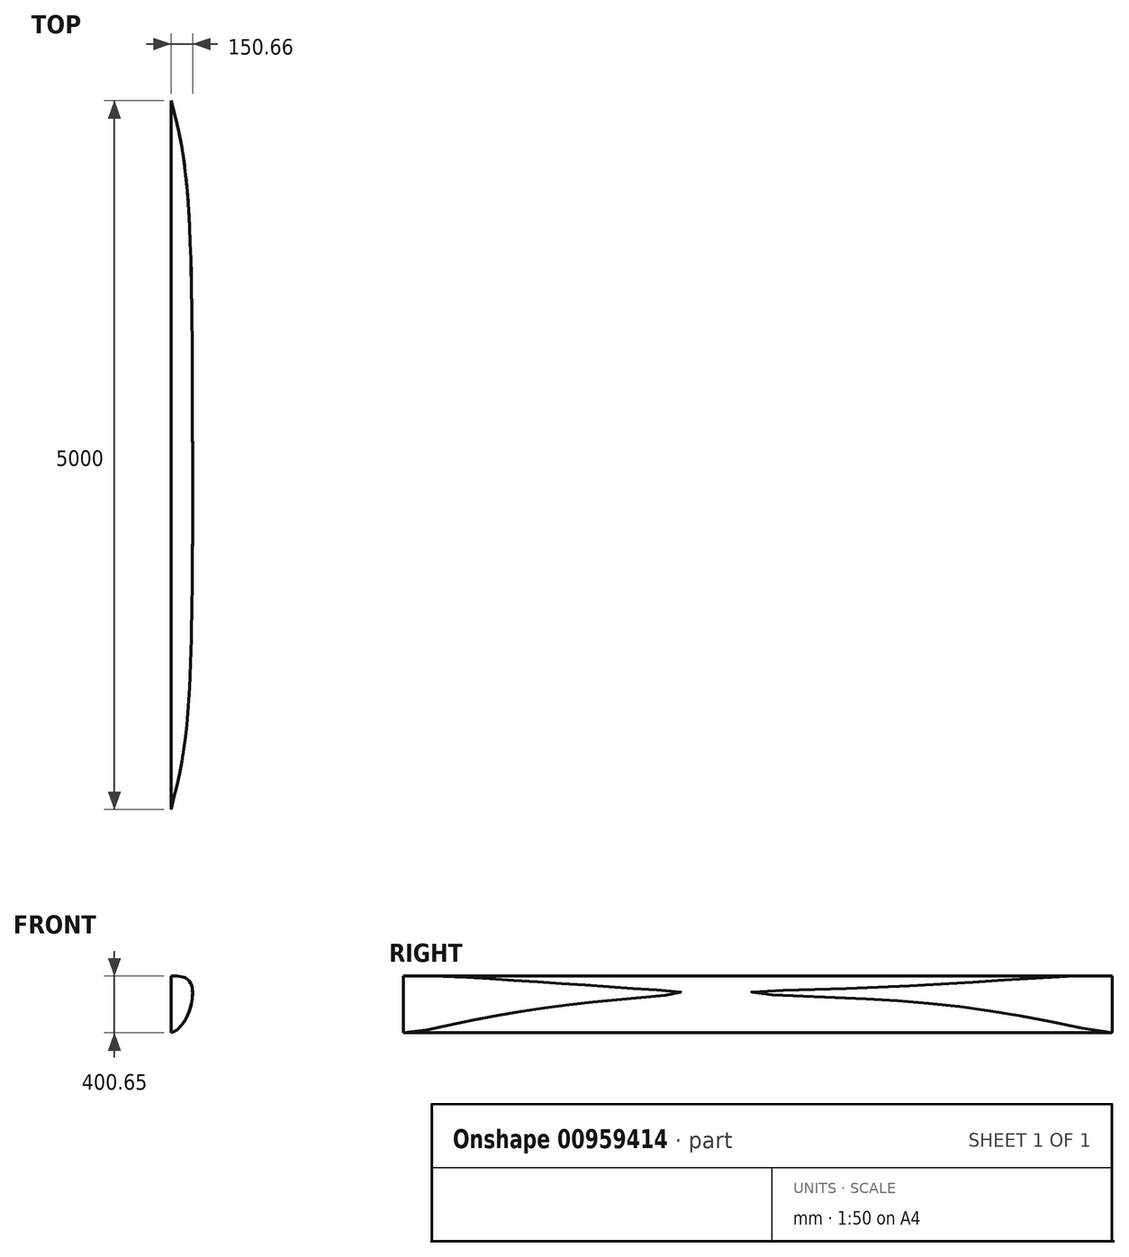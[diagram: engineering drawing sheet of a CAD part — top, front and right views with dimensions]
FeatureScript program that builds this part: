
annotation { "Feature Type Name" : "Feature", "Feature Type Description" : "" }
export const myFeature = defineFeature(function(context is Context, id is Id, definition is map)
    precondition{}
    {
        {
            var Q0;
            Q0=qCreatedBy(makeId("Top.planeOp"),FACE);
            var sketch = newSketch(context, id + "F0", { "sketchPlane" : qUnion([Q0])});
            skLineSegment(sketch, "E0", {"start": v(0, 0) * mm, "end": v(0, -2700) * mm});
            skLineSegment(sketch, "E1", {"start": v(0, 0) * mm, "end": v(0, 2300) * mm});
            skLineSegment(sketch, "E2", {"start": v(0, 1800) * mm, "end": v(100, 1800) * mm, "construction": true});
            skLineSegment(sketch, "E3", {"start": v(0, -2200) * mm, "end": v(100, -2200) * mm, "construction": true});
            skLineSegment(sketch, "E4", {"start": v(0, 0) * mm, "end": v(150, 0) * mm, "construction": true});
            skSolve(sketch);
        }
        {
            var Q0;
            Q0=qCreatedBy(makeId("Right.planeOp"),FACE);
            var sketch = newSketch(context, id + "F1", { "sketchPlane" : qUnion([Q0])});
            skLineSegment(sketch, "E5", {"start": v(0, 0) * mm, "end": v(0, -300) * mm, "construction": true});
            skLineSegment(sketch, "E6", {"start": v(1800, 0) * mm, "end": v(1800, -250) * mm, "construction": true});
            skLineSegment(sketch, "E7", {"start": v(-2200, 0) * mm, "end": v(-2200, -250) * mm, "construction": true});
            skSolve(sketch);
        }
        {
            var Q0;
            Q0=qCreatedBy(makeId("Front.planeOp"),FACE);
            var sketch = newSketch(context, id + "F2", { "sketchPlane" : qUnion([Q0])});
            skFitSpline(sketch, "E8", {"points": [v(0, 100) * mm, v(95, 90) * mm, v(150, 0) * mm, v(0, -300) * mm], "startDerivative": vector(370.55, 15) * mm, "endDerivative": vector(-679.9, -235.19) * mm});
            skLineSegment(sketch, "E9", {"start": v(0, 100) * mm, "end": v(0, -300) * mm});
            skLineSegment(sketch, "E10", {"start": v(0, 100) * mm, "end": v(0, 90) * mm, "construction": true});
            skLineSegment(sketch, "E11", {"start": v(0, 90) * mm, "end": v(95, 90) * mm, "construction": true});
            skSolve(sketch);
        }
        {
            var Q0;
            Q0=qCreatedBy(makeId("Right.planeOp"),FACE);
            var sketch = newSketch(context, id + "F3", { "sketchPlane" : qUnion([Q0])});
            skLineSegment(sketch, "E12", {"start": v(-2700, 0) * mm, "end": v(-2700, -122.66) * mm});
            skFitSpline(sketch, "E13", {"points": [v(-2700, 0) * mm, v(-2700, -122.66) * mm, v(-2200, -250) * mm, v(0, -303.82) * mm, v(1800, -250) * mm, v(2241.6, -122.66) * mm, v(2300, 0) * mm], "startDerivative": vector(-468.48, -1833.42) * mm, "endDerivative": vector(63.31, 1731.94) * mm});
            skSolve(sketch);
        }
        {
            var Q0;
            Q0=qCreatedBy(makeId("Top.planeOp"),FACE);
            var sketch = newSketch(context, id + "F4", { "sketchPlane" : qUnion([Q0])});
            skFitSpline(sketch, "E14", {"points": [v(0, -2700) * mm, v(100, -2200) * mm, v(150, 0) * mm, v(100, 1800) * mm, v(0, 2300) * mm], "startDerivative": vector(591.73, 2733.7) * mm, "endDerivative": vector(-653.13, 2340.85) * mm});
            skLineSegment(sketch, "E15", {"start": v(0, -2700) * mm, "end": v(0, 2300) * mm});
            skSolve(sketch);
        }
        {
            var Q0;
            Q0=makeQuery(id+"F2.imprint","IMPRINT",FACE,{"disambiguationData":[TD([[makeQuery(id+"F2.imprint","IMPRINT",EDGE,{"derivedFrom":sQuery(id+"F2.wireOp",EDGE,"E8")}),-1.0]])]});
            extrude(context, id + "F5", {"entities" : qUnion([Q0]), "endBound" : BoundingType.SYMMETRIC, "depth" : 11380 * mm, "offsetDistance" : 25 * mm});
        }
        {
            var Q0;
            Q0=makeQuery(id+"F4.imprint","IMPRINT",FACE,{"disambiguationData":[TD([[makeQuery(id+"F4.imprint","IMPRINT",EDGE,{"derivedFrom":sQuery(id+"F4.wireOp",EDGE,"E14")}),1.0]])]});
            extrude(context, id + "F6", {"entities" : qUnion([Q0]), "endBound" : BoundingType.SYMMETRIC, "oppositeDirection" : true, "depth" : 800 * mm, "offsetDistance" : 25 * mm});
        }
        {
            var Q0;
            Q0=sQuery(id+"F3.wireOp",EDGE,"E13");
            extrude(context, id + "F7", {"bodyType" : ToolBodyType.SURFACE, "surfaceEntities" : qUnion([Q0]), "depth" : 50 * mm, "offsetDistance" : 25 * mm});
        }
        {
            var Q0;
            Q0=makeQuery(id+"F6.opExtrude","SWEPT_BODY",BODY,{"disambiguationData":[OSD([sQuery(id+"F4.wireOp",EDGE,"E14"),sQuery(id+"F4.wireOp",EDGE,"E15")])]});
            var Q1;
            Q1=makeQuery(id+"F5.opExtrude","SWEPT_BODY",BODY,{"disambiguationData":[OSD([sQuery(id+"F2.wireOp",EDGE,"E8"),sQuery(id+"F2.wireOp",EDGE,"E9")])]});
            booleanBodies(context, id + "F8", {"operationType" : BooleanOperationType.INTERSECTION, "tools" : qUnion([Q0, Q1])});
        }
    });
